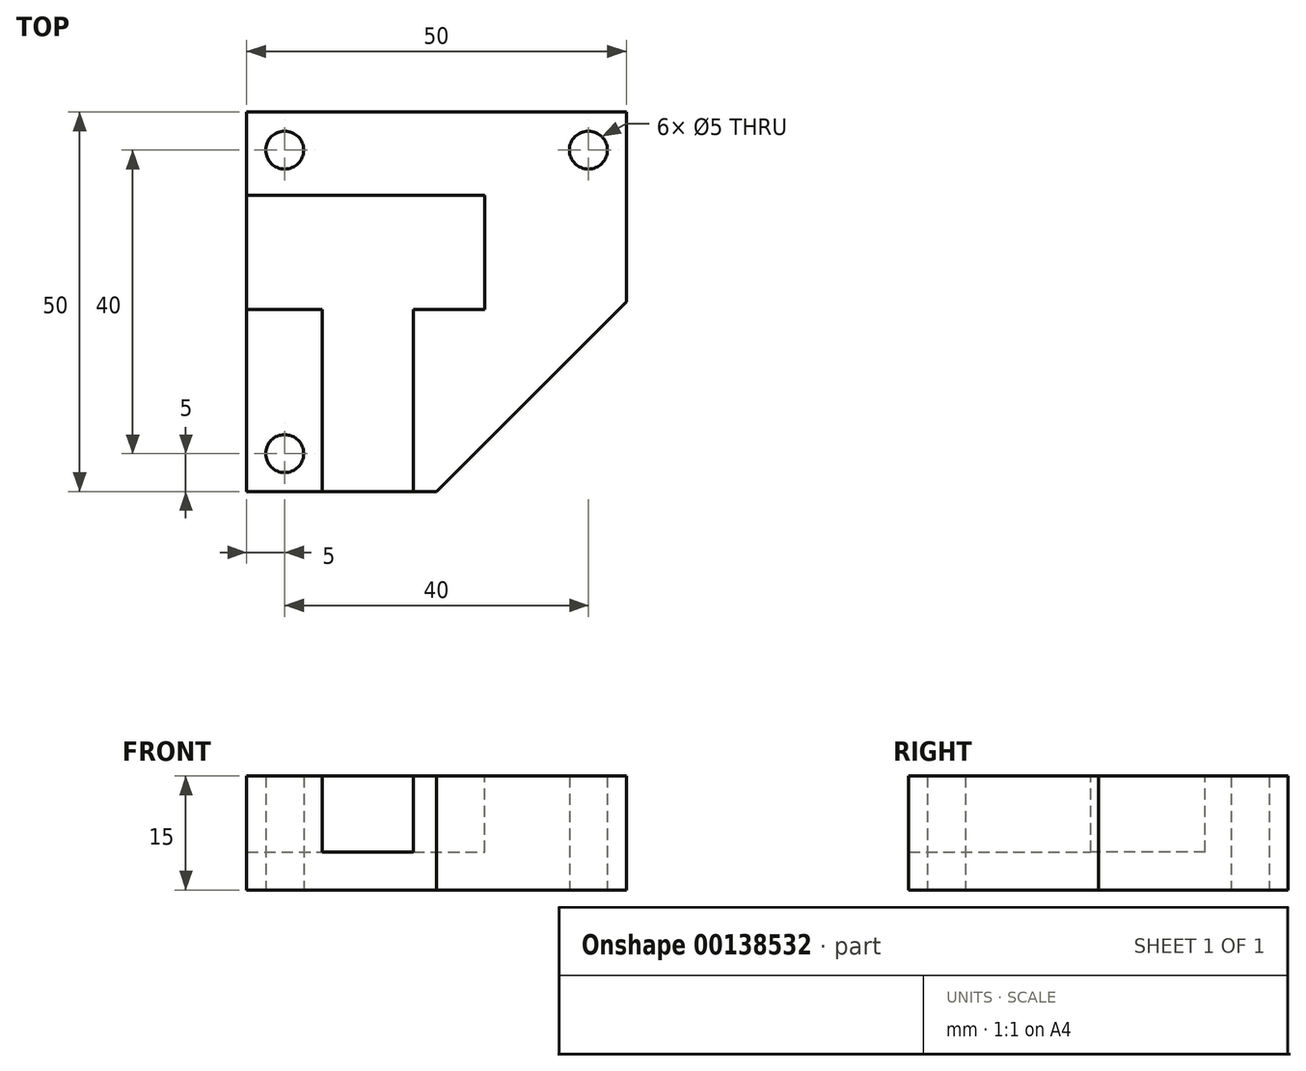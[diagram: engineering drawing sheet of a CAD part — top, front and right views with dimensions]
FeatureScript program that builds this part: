
annotation { "Feature Type Name" : "Feature", "Feature Type Description" : "" }
export const myFeature = defineFeature(function(context is Context, id is Id, definition is map)
    precondition{}
    {
        {
            var Q0;
            Q0=qCreatedBy(makeId("Top.planeOp"),FACE);
            var sketch = newSketch(context, id + "F0", { "sketchPlane" : qUnion([Q0])});
            skLineSegment(sketch, "E0", {"start": v(0, 50) * mm, "end": v(0, 0) * mm});
            skLineSegment(sketch, "E1", {"start": v(0, 0) * mm, "end": v(25, 0) * mm});
            skLineSegment(sketch, "E2", {"start": v(25, 0) * mm, "end": v(50, 25) * mm});
            skLineSegment(sketch, "E3", {"start": v(50, 25) * mm, "end": v(50, 50) * mm});
            skLineSegment(sketch, "E4", {"start": v(50, 50) * mm, "end": v(0, 50) * mm});
            skCircle(sketch, "E5", {"center": v(5, 45) * mm, "radius": 2.5 * mm});
            skCircle(sketch, "E6", {"center": v(45, 45) * mm, "radius": 2.5 * mm});
            skCircle(sketch, "E7", {"center": v(5, 5) * mm, "radius": 2.5 * mm});
            skLineSegment(sketch, "E8", {"start": v(5, 45) * mm, "end": v(5, 50) * mm, "construction": true});
            skLineSegment(sketch, "E9", {"start": v(5, 45) * mm, "end": v(0, 45) * mm, "construction": true});
            skLineSegment(sketch, "E10", {"start": v(45, 45) * mm, "end": v(45, 50) * mm, "construction": true});
            skLineSegment(sketch, "E11", {"start": v(45, 45) * mm, "end": v(50, 45) * mm, "construction": true});
            skLineSegment(sketch, "E12", {"start": v(5, 5) * mm, "end": v(5, 0) * mm, "construction": true});
            skLineSegment(sketch, "E13", {"start": v(5, 5) * mm, "end": v(0, 5) * mm, "construction": true});
            skSolve(sketch);
        }
        {
            var Q0;
            Q0=makeQuery(id+"F0.imprint","IMPRINT",FACE,{"disambiguationData":[TD([[makeQuery(id+"F0.imprint","IMPRINT",EDGE,{"derivedFrom":sQuery(id+"F0.wireOp",EDGE,"E0")}),1.0]])]});
            extrude(context, id + "F1", {"entities" : qUnion([Q0]), "depth" : 15 * mm});
        }
        {
            var Q0;
            Q0=makeQuery(id+"F1.opExtrude","CAP_FACE",FACE,{"disambiguationData":[OSD([sQuery(id+"F0.wireOp",EDGE,"E0"),sQuery(id+"F0.wireOp",EDGE,"E1"),sQuery(id+"F0.wireOp",EDGE,"E2"),sQuery(id+"F0.wireOp",EDGE,"E3"),sQuery(id+"F0.wireOp",EDGE,"E4"),sQuery(id+"F0.wireOp",EDGE,"E5"),sQuery(id+"F0.wireOp",EDGE,"E6"),sQuery(id+"F0.wireOp",EDGE,"E7")])],"isStart":false});
            var sketch = newSketch(context, id + "F2", { "sketchPlane" : qUnion([Q0])});
            skLineSegment(sketch, "E14.bottom", {"start": v(0, 39.07) * mm, "end": v(31.32, 39.07) * mm});
            skLineSegment(sketch, "E14.top", {"start": v(0, 24) * mm, "end": v(31.32, 24) * mm});
            skLineSegment(sketch, "E14.left", {"start": v(0, 39.07) * mm, "end": v(0, 24) * mm});
            skLineSegment(sketch, "E14.right", {"start": v(31.32, 39.07) * mm, "end": v(31.32, 24) * mm});
            skLineSegment(sketch, "E15.bottom", {"start": v(9.92, 0) * mm, "end": v(21.92, 0) * mm});
            skLineSegment(sketch, "E15.top", {"start": v(9.92, 24) * mm, "end": v(21.92, 24) * mm});
            skLineSegment(sketch, "E15.left", {"start": v(9.92, 0) * mm, "end": v(9.92, 24) * mm});
            skLineSegment(sketch, "E15.right", {"start": v(21.92, 0) * mm, "end": v(21.92, 24) * mm});
            skSolve(sketch);
        }
        {
            var Q0;
            Q0=makeQuery(id+"F2.imprint","IMPRINT",FACE,{"disambiguationData":[TD([[makeQuery(id+"F2.imprint","IMPRINT",EDGE,{"derivedFrom":sQuery(id+"F2.wireOp",EDGE,"E14.bottom")}),-1.0]])]});
            var Q1;
            Q1=makeQuery(id+"F2.imprint","IMPRINT",FACE,{"disambiguationData":[TD([[makeQuery(id+"F2.imprint","IMPRINT",EDGE,{"derivedFrom":sQuery(id+"F2.wireOp",EDGE,"E15.bottom")}),1.0]])]});
            extrude(context, id + "F3", {"entities" : qUnion([Q0, Q1]), "operationType" : NewBodyOperationType.REMOVE, "oppositeDirection" : true, "depth" : 10 * mm});
        }
    });
